# Revit family: GC_ProgettoFinale_Famiglia2
name_source: partatom
category: Generic Models
revit_build: Autodesk Revit 2016 (Build: 20150714_1515(x64)
units: mm (PartAtom-declared; Revit-internal decimal feet)

## family parameters
Always vertical = Yes
Can host rebar = No
Cut with Voids When Loaded = No
Part Type = Normal
Room Calculation Point = No
Round Connector Dimension = Use Diameter
Shared = No
Work Plane-Based = No

## types (11) — shared parameters

## per-type parameters (varying)
| type | Altezza | Letto | Sedia | Tavolo |
| + 0.25 | 250 mm | 1500 mm  [stored 4.92126 ft] | 1800 mm  [stored 5.90551 ft] | 400 mm  [stored 1.31234 ft] |
| + 0.50 | 250 mm | 1500 mm  [stored 4.92126 ft] | 1800 mm  [stored 5.90551 ft] | 400 mm  [stored 1.31234 ft] |
| + 0.75 | 250 mm | 900 mm  [stored 2.95276 ft] | 1000 mm  [stored 3.28084 ft] | 1200 mm |
| + 1.00 | 250 mm | 900 mm  [stored 2.95276 ft] | 1000 mm  [stored 3.28084 ft] | 400 mm  [stored 1.31234 ft] |
| + 1.25 | 250 mm | 900 mm  [stored 2.95276 ft] | 1000 mm  [stored 3.28084 ft] | 400 mm  [stored 1.31234 ft] |
| + 1.50 | 250 mm | 1000 mm  [stored 3.28084 ft] | 1000 mm  [stored 3.28084 ft] | 500 mm  [stored 1.64042 ft] |
| + 1.75 | 250 mm | 1100 mm | 1000 mm  [stored 3.28084 ft] | 500 mm  [stored 1.64042 ft] |
| + 2.00 | 250 mm | 1200 mm | 1100 mm | 600 mm |
| + 2.25 | 250 mm | 1300 mm  [stored 4.26509 ft] | 1200 mm | 700 mm  [stored 2.29659 ft] |
| + 2.50 | 250 mm | 1400 mm  [stored 4.59318 ft] | 1300 mm  [stored 4.26509 ft] | 800 mm  [stored 2.62467 ft] |
| + 2.75 | 0 mm  [stored 0 ft] | 1500 mm  [stored 4.92126 ft] | 1400 mm  [stored 4.59318 ft] | 900 mm  [stored 2.95276 ft] |

note: [stored X ft] marks values corroborated as IEEE doubles in the binary element streams (Revit-internal decimal feet)

## geometry (parser evidence)
native form markers: Sweep x3
no freeform markers — native parametric forms only
